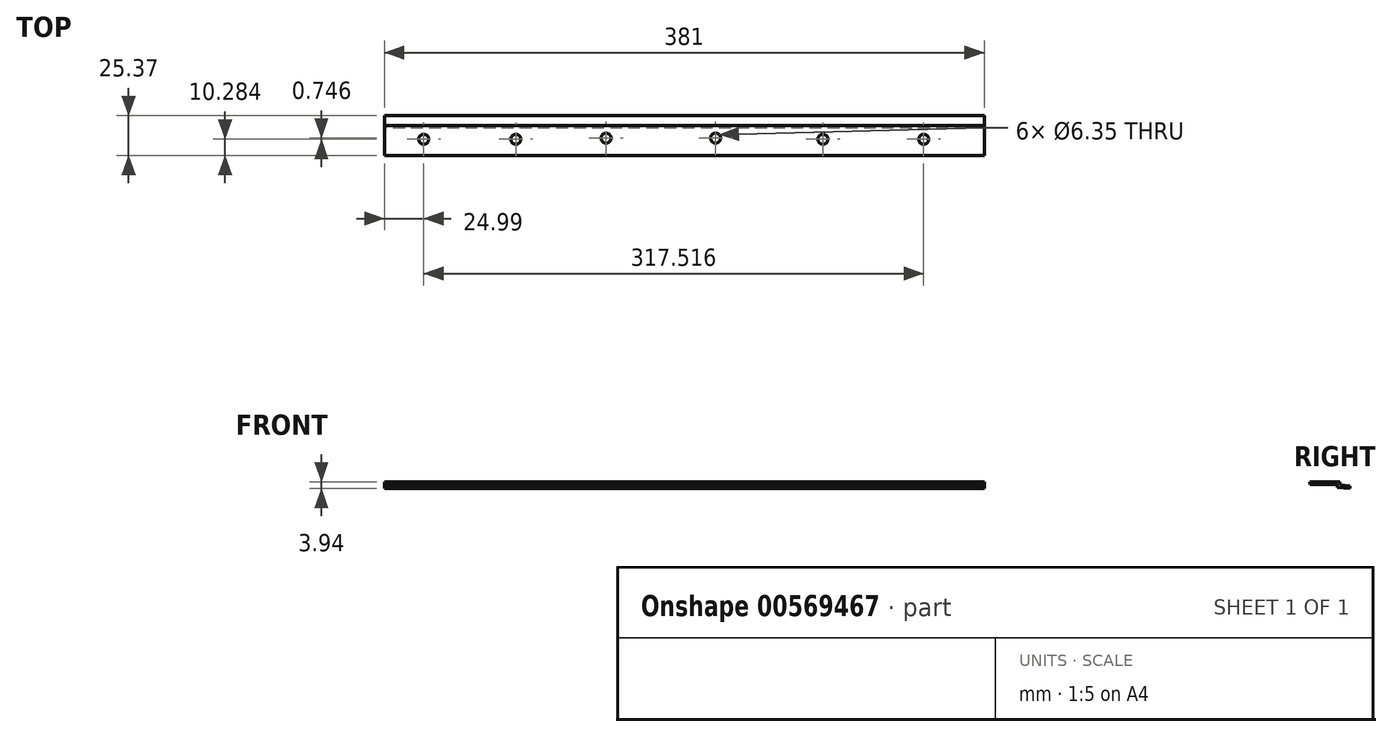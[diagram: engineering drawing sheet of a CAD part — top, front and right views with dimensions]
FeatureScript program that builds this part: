
annotation { "Feature Type Name" : "Feature", "Feature Type Description" : "" }
export const myFeature = defineFeature(function(context is Context, id is Id, definition is map)
    precondition{}
    {
        {
            var Q0;
            Q0=qCreatedBy(makeId("Right.planeOp"),FACE);
            var sketch = newSketch(context, id + "F0", { "sketchPlane" : qUnion([Q0])});
            skLineSegment(sketch, "E0", {"start": v(0, 0) * mm, "end": v(17.53, 0) * mm});
            skLineSegment(sketch, "E1", {"start": v(17.53, 0) * mm, "end": v(17.53, -1.7) * mm});
            skLineSegment(sketch, "E2", {"start": v(17.53, -1.7) * mm, "end": v(25.37, -2.42) * mm});
            skLineSegment(sketch, "E3", {"start": v(25.37, -2.42) * mm, "end": v(25.37, -0.9) * mm});
            skLineSegment(sketch, "E4", {"start": v(25.37, -0.9) * mm, "end": v(19.05, -0.3) * mm});
            skLineSegment(sketch, "E5", {"start": v(0, 0) * mm, "end": v(0, 1.52) * mm});
            skLineSegment(sketch, "E6", {"start": v(0, 1.52) * mm, "end": v(19.05, 1.52) * mm});
            skLineSegment(sketch, "E7", {"start": v(19.05, -0.3) * mm, "end": v(19.05, 1.52) * mm});
            skSolve(sketch);
        }
        {
            var Q0;
            Q0=makeQuery(id+"F0.imprint","IMPRINT",FACE,{"disambiguationData":[TD([[makeQuery(id+"F0.imprint","IMPRINT",EDGE,{"derivedFrom":sQuery(id+"F0.wireOp",EDGE,"E0")}),1.0]])]});
            extrude(context, id + "F1", {"entities" : qUnion([Q0]), "depth" : 381 * mm, "offsetDistance" : 25.4 * mm});
        }
        {
            var Q0;
            Q0=makeQuery(id+"F1.opExtrude","SWEPT_FACE",FACE,{"disambiguationData":[OSD([sQuery(id+"F0.wireOp",EDGE,"E6")])]});
            var sketch = newSketch(context, id + "F2", { "sketchPlane" : qUnion([Q0])});
            skCircle(sketch, "E8", {"center": v(24.99, 10.33) * mm, "radius": 2.54 * mm});
            skCircle(sketch, "E9", {"center": v(83.52, 10.33) * mm, "radius": 2.54 * mm});
            skCircle(sketch, "E10", {"center": v(210.36, 11.03) * mm, "radius": 2.54 * mm});
            skCircle(sketch, "E11", {"center": v(140.8, 11.03) * mm, "radius": 2.54 * mm});
            skCircle(sketch, "E12", {"center": v(278.54, 10.28) * mm, "radius": 2.54 * mm});
            skCircle(sketch, "E13", {"center": v(342.5, 10.28) * mm, "radius": 2.54 * mm});
            skSolve(sketch);
        }
        {
            var Q0;
            Q0=sQuery(id+"F2.wireOp",VERTEX,"E9.center");
            var Q1;
            Q1=sQuery(id+"F2.wireOp",VERTEX,"E11.center");
            var Q2;
            Q2=sQuery(id+"F2.wireOp",VERTEX,"E10.center");
            var Q3;
            Q3=sQuery(id+"F2.wireOp",VERTEX,"E12.center");
            var Q4;
            Q4=sQuery(id+"F2.wireOp",VERTEX,"E13.center");
            var Q5;
            Q5=sQuery(id+"F2.wireOp",VERTEX,"E8.center");
            var Q6;
            Q6=makeQuery(id+"F1.opExtrude","SWEPT_BODY",BODY,{"disambiguationData":[OSD([sQuery(id+"F0.wireOp",EDGE,"E0"),sQuery(id+"F0.wireOp",EDGE,"E1"),sQuery(id+"F0.wireOp",EDGE,"E2"),sQuery(id+"F0.wireOp",EDGE,"E3"),sQuery(id+"F0.wireOp",EDGE,"E4"),sQuery(id+"F0.wireOp",EDGE,"E5"),sQuery(id+"F0.wireOp",EDGE,"E6"),sQuery(id+"F0.wireOp",EDGE,"E7")])]});
            hole(context, id + "F3", {"style" : HoleStyle.SIMPLE, "endStyle" : HoleEndStyle.THROUGH, "holeDiameter" : 6.35 * mm, "majorDiameter" : 6.35 * mm, "isTappedThrough" : true, "tappedDepth" : 12.7 * mm, "tapClearance" : 3, "locations" : qUnion([Q0, Q1, Q2, Q3, Q4, Q5]), "scope" : qUnion([Q6])});
        }
    });
